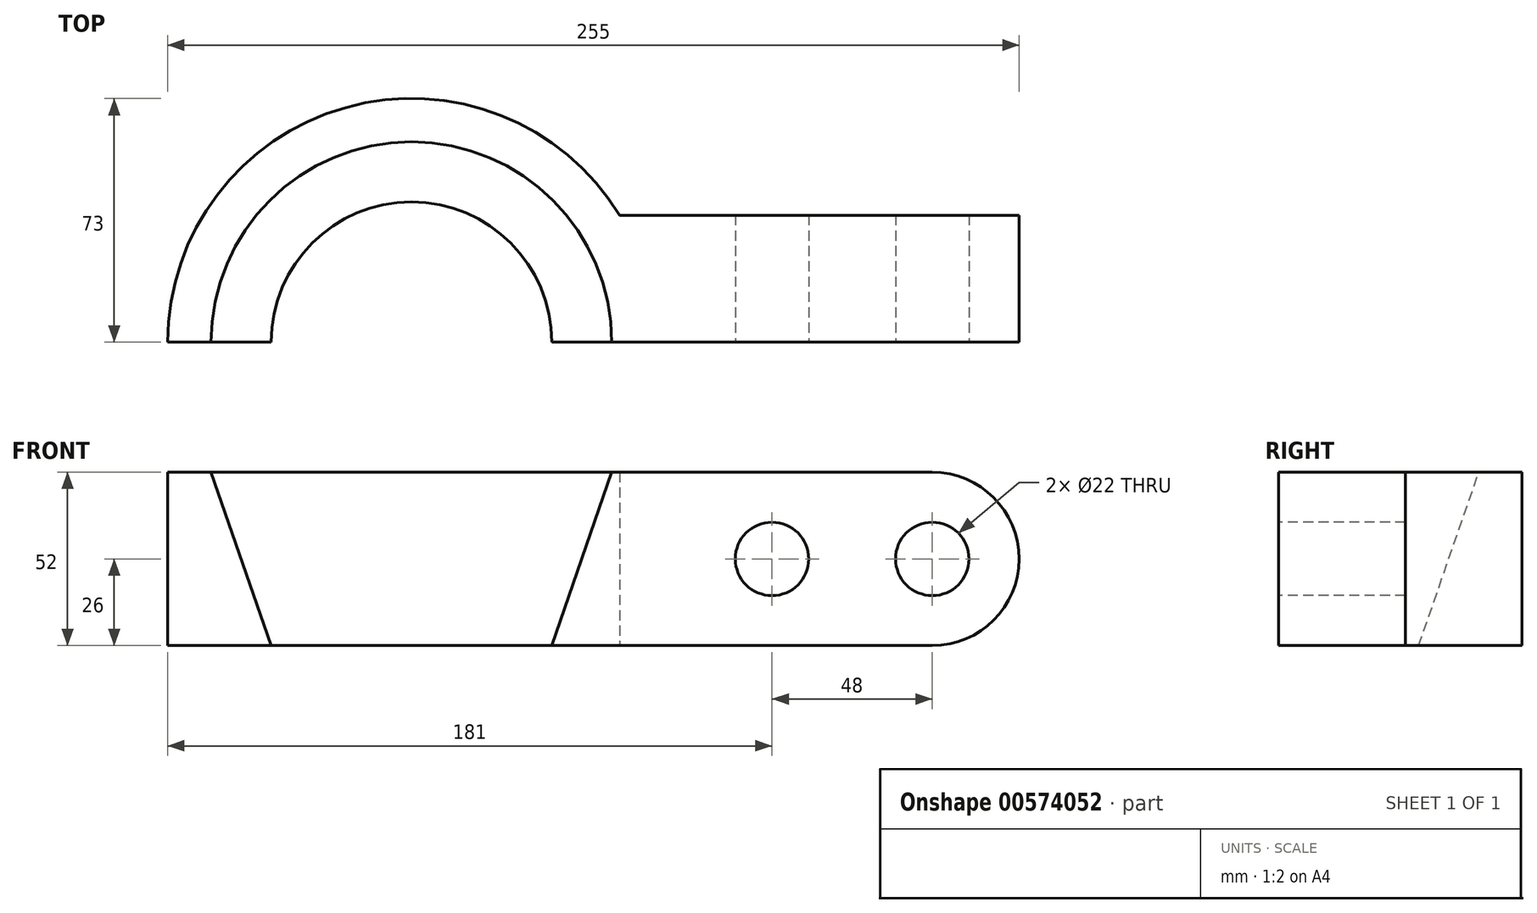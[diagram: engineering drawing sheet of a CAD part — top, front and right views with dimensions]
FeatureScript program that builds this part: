
annotation { "Feature Type Name" : "Feature", "Feature Type Description" : "" }
export const myFeature = defineFeature(function(context is Context, id is Id, definition is map)
    precondition{}
    {
        {
            var Q0;
            Q0=qCreatedBy(makeId("Top.planeOp"),FACE);
            var sketch = newSketch(context, id + "F0", { "sketchPlane" : qUnion([Q0])});
            skArc(sketch, "E0", {"start": v(-73, 0) * mm, "mid": v(-19.73, 70.28) * mm, "end": v(62.33, 38) * mm});
            skLineSegment(sketch, "E1", {"start": v(62.33, 38) * mm, "end": v(182, 38) * mm});
            skLineSegment(sketch, "E2", {"start": v(182, 38) * mm, "end": v(182, 0) * mm});
            skLineSegment(sketch, "E3", {"start": v(182, 0) * mm, "end": v(-73, 0) * mm});
            skSolve(sketch);
        }
        {
            var Q0;
            Q0 = qSketchRegion(id + "F0", true);
            extrude(context, id + "F1", {"entities" : qUnion([Q0]), "depth" : 52 * mm, "offsetDistance" : 25 * mm});
        }
        {
            var Q0;
            Q0=makeQuery(id+"F1.opExtrude","SWEPT_FACE",FACE,{"disambiguationData":[OSD([sQuery(id+"F0.wireOp",EDGE,"E3")])]});
            var sketch = newSketch(context, id + "F2", { "sketchPlane" : qUnion([Q0])});
            skLineSegment(sketch, "E4", {"start": v(0, 52) * mm, "end": v(0, 0) * mm});
            skLineSegment(sketch, "E5", {"start": v(0, 0) * mm, "end": v(42, 0) * mm});
            skLineSegment(sketch, "E6", {"start": v(42, 0) * mm, "end": v(60, 52) * mm});
            skLineSegment(sketch, "E7", {"start": v(60, 52) * mm, "end": v(0, 52) * mm});
            skSolve(sketch);
        }
        {
            var Q0;
            Q0 = qSketchRegion(id + "F2", true);
            var Q1;
            Q1=sQuery(id+"F2.wireOp",EDGE,"E4");
            revolve(context, id + "F3", {"operationType" : NewBodyOperationType.REMOVE, "entities" : qUnion([Q0]), "axis" : qUnion([Q1]), "revolveType" : RevolveType.FULL, "oppositeDirection" : true});
        }
        {
            var Q0;
            Q0=makeQuery(id+"F1.opExtrude","CAP_EDGE",EDGE,{"disambiguationData":[OSD([sQuery(id+"F0.wireOp",EDGE,"E2")])],"isStart":false});
            var Q1;
            Q1=makeQuery(id+"F1.opExtrude","CAP_EDGE",EDGE,{"disambiguationData":[OSD([sQuery(id+"F0.wireOp",EDGE,"E2")])],"isStart":true});
            fillet(context, id + "F4", {"entities" : qUnion([Q0, Q1]), "radius" : 26 * mm, "tangentPropagation" : true, "allowEdgeOverflow" : false});
        }
        {
            var Q0;
            {var subQ0=sQuery(id+"F0.wireOp",EDGE,"E3");var subQ1=sQuery(id+"F0.wireOp",EDGE,"E2");Q0=makeQuery(id+"F3.boolean.opBoolean","SPLIT",FACE,{"disambiguationData":[TD([makeQuery(id+"F1.opExtrude","SWEPT_FACE",FACE,{"disambiguationData":[OSD([subQ1])]})])],"derivedFrom":makeQuery(id+"F1.opExtrude","SWEPT_FACE",FACE,{"disambiguationData":[OSD([subQ0])]})});}
            var sketch = newSketch(context, id + "F5", { "sketchPlane" : qUnion([Q0])});
            skCircle(sketch, "E8", {"center": v(108, 26) * mm, "radius": 11 * mm});
            skCircle(sketch, "E9", {"center": v(156, 26) * mm, "radius": 11 * mm});
            skLineSegment(sketch, "E10", {"start": v(-10.65, 26) * mm, "end": v(183.86, 26) * mm, "construction": true});
            skSolve(sketch);
        }
        {
            var Q0;
            Q0 = qSketchRegion(id + "F5", true);
            extrude(context, id + "F6", {"entities" : qUnion([Q0]), "operationType" : NewBodyOperationType.REMOVE, "oppositeDirection" : true, "depth" : 100 * mm, "offsetDistance" : 25 * mm});
        }
    });
